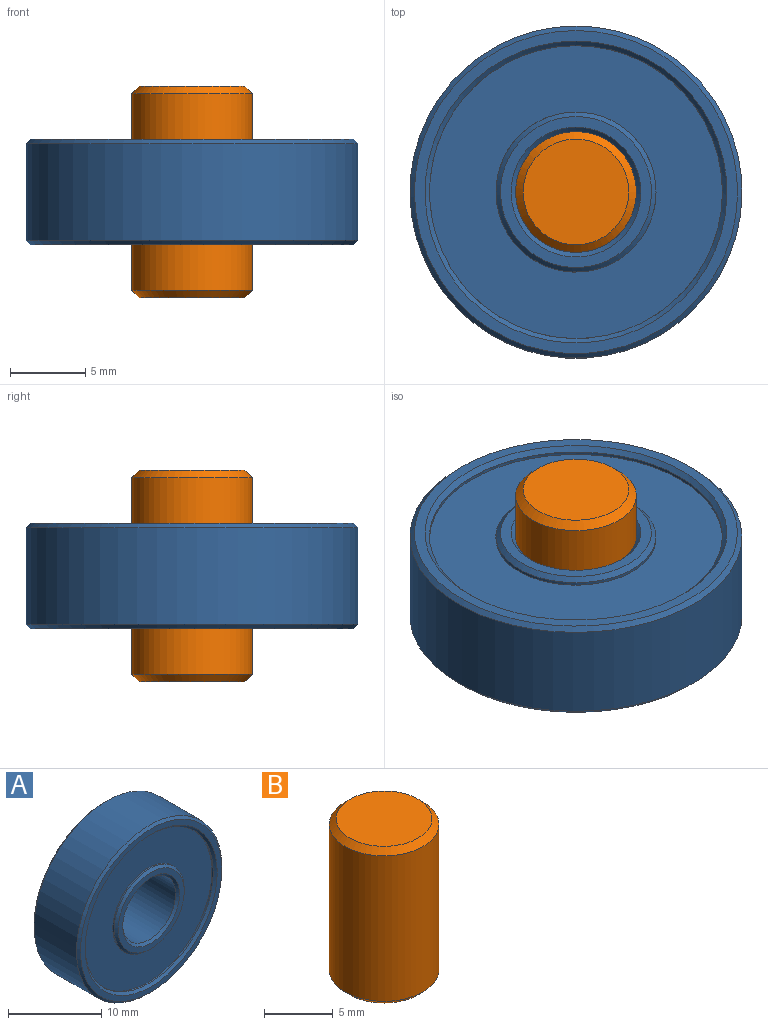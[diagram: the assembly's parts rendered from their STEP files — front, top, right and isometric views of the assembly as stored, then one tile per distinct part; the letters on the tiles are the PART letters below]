
ASSEMBLY  parts=2 mates=1
PART A: 20 faces, bbox 22x7x22 mm
  f0: cylinder r=9.7mm len=19.4mm, axis (0,1,0), area 12.2mm2, adj f11,f14
  f1: cylinder r=9.7mm len=19.4mm, axis (0,1,0), area 12.2mm2, adj f10,f18
  f2: cylinder r=11mm len=22mm, axis (0,1,0), area 442.3mm2, adj f15,f19
  f3: plane 21.4x21.4mm, normal (0,-1,0), area 45.5mm2, adj f18,f19
  f4: plane 21.4x21.4mm, normal (0,1,0), area 45.5mm2, adj f14,f15
  f5: cylinder r=5.3mm len=10.6mm, axis (0,1,0), area 6.7mm2, adj f11,f13
  f6: cylinder r=4mm len=8mm, axis (0,1,0), area 160.8mm2, adj f12,f16
  f7: cylinder r=5.3mm len=10.6mm, axis (0,1,0), area 6.7mm2, adj f10,f17
  f8: plane 10x10mm, normal (0,-1,0), area 20.5mm2, adj f16,f17
  f9: plane 10x10mm, normal (0,1,0), area 20.5mm2, adj f12,f13
  f10: plane 19.4x19.4mm, normal (0,-1,0), area 207.3mm2, adj f1,f7
  f11: plane 19.4x19.4mm, normal (0,1,0), area 207.3mm2, adj f0,f5
  f12: cone r=4.3mm half-angle=45deg, axis (0,1,0), area 11.1mm2, adj f6,f9
  f13: cone r=5.3mm half-angle=45deg, axis (0,-1,0), area 13.7mm2, adj f5,f9
  f14: cone r=10mm half-angle=45deg, axis (0,1,0), area 26.3mm2, adj f0,f4
  f15: cone r=11mm half-angle=45deg, axis (0,-1,0), area 28.9mm2, adj f2,f4
  f16: cone r=4mm half-angle=45deg, axis (0,-1,0), area 11.1mm2, adj f6,f8
  f17: cone r=5mm half-angle=45deg, axis (0,1,0), area 13.7mm2, adj f7,f8
  f18: cone r=9.7mm half-angle=45deg, axis (0,-1,0), area 26.3mm2, adj f1,f3
  f19: cone r=10.7mm half-angle=45deg, axis (0,1,0), area 28.9mm2, adj f2,f3
PART B: 5 faces, bbox 8x8x14 mm
  f0: cylinder r=4mm len=13mm, axis (0,0,-1), area 326.7mm2, adj f3,f4
  f1: plane 7x7mm, normal (0,0,1), area 38.5mm2, adj f3
  f2: plane 7x7mm, normal (0,0,-1), area 38.5mm2, adj f4
  f3: cone r=3.5mm half-angle=45deg, axis (0,0,-1), area 16.7mm2, adj f0,f1
  f4: cone r=4mm half-angle=45deg, axis (0,0,1), area 16.7mm2, adj f0,f2
PLACE A rot(axis=(1,0,0),90deg) t=(0,0,7)mm
PLACE B at identity fixed
MATE fastened B.f0 <-> A.f0  axis (0,0,-1) through (0,0,7)mm
